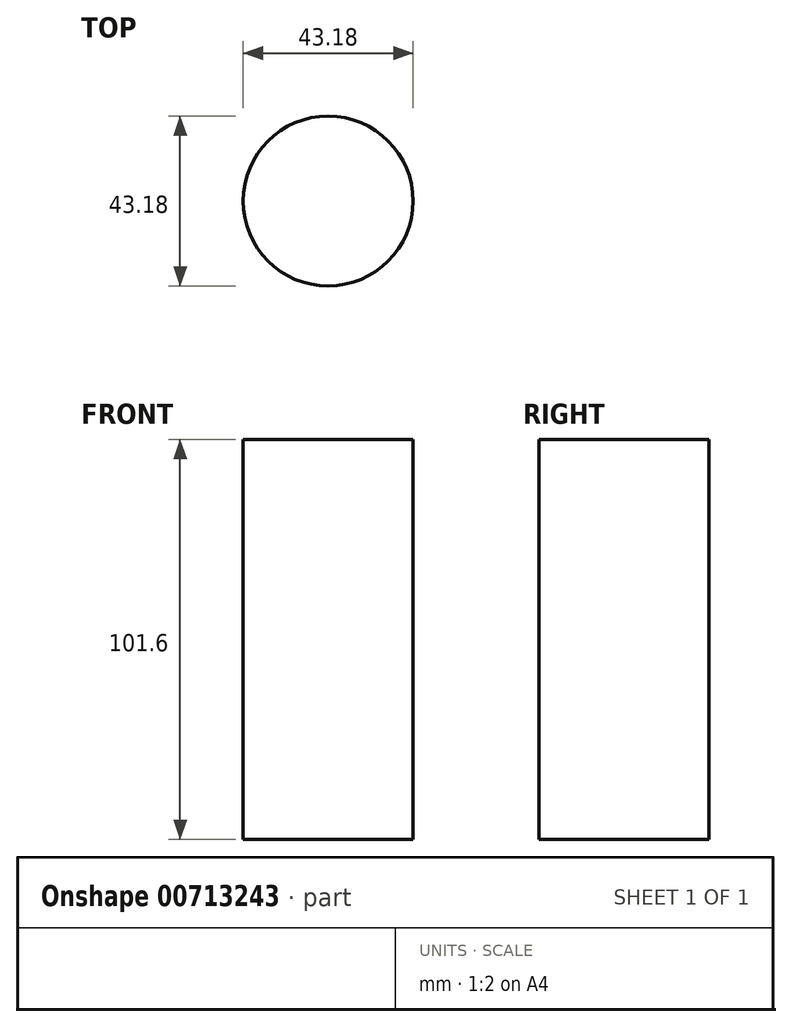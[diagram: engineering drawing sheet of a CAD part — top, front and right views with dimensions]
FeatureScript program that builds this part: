
annotation { "Feature Type Name" : "Feature", "Feature Type Description" : "" }
export const myFeature = defineFeature(function(context is Context, id is Id, definition is map)
    precondition{}
    {
        {
            var Q0;
            Q0=qCreatedBy(makeId("Top.planeOp"),FACE);
            var sketch = newSketch(context, id + "F0", { "sketchPlane" : qUnion([Q0])});
            skCircle(sketch, "E0", {"center": v(0, 0) * mm, "radius": 21.59 * mm});
            skSolve(sketch);
        }
        {
            var Q0;
            Q0=makeQuery(id+"F0.imprint","IMPRINT",FACE,{"disambiguationData":[TD([[makeQuery(id+"F0.imprint","IMPRINT",EDGE,{"derivedFrom":sQuery(id+"F0.wireOp",EDGE,"E0")}),1.0]])]});
            extrude(context, id + "F1", {"entities" : qUnion([Q0]), "depth" : 101.6 * mm, "offsetDistance" : 25.4 * mm});
        }
    });
